# Revit family: R1100-PR
name_source: partatom
category: Plumbing Fixtures
revit_build: Autodesk Revit 2018 (Build: 20170223_1515(x64)
units: mm (PartAtom-declared; Revit-internal decimal feet)

## family parameters
Cut with Voids When Loaded = No
Host = Face
Part Type = Normal
Room Calculation Point = No
Round Connector Dimension = Use Radius
Shared = No

## types (5) — shared parameters
Default Elevation = 0' - 0"
Description = PROMENADE DECK DRAIN
Floor Drain Material = Paint - Sherwin Williams Paint - #952C2A - Bellwood Red
Manufacturer = MIFAB
Model = R1100-PR
Top Assembly Adjustment = 0' - 3"
URL = WWW.MIFAB.COM
zero-valued in all types: CWFU, WFU

## per-type parameters (varying)
| type | Bottom Adjustmen | Pipe Diameter | Pipe Radius |
| 6" Drain Pipe Size | 0' - 5" | 0' - 6" | 0' - 3" |
| 5" Drain Pipe Size | 0' - 5" | 0' - 5" | 0' - 2 1/2" |
| 4" Drain Pipe Size | 0' - 4 1/2" | 0' - 4" | 0' - 2" |
| 3" Drain Pipe Size | 0' - 5" | 0' - 3" | 0' - 1 1/2" |
| 2" Drain Pipe Size | 0' - 5" | 0' - 2" | 0' - 1" |

## geometry (parser evidence)
native form markers: Blend x2, Sweep x6
no freeform markers — native parametric forms only
